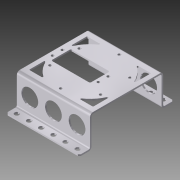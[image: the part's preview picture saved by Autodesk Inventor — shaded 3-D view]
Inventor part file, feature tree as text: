
AUTODESK INVENTOR PART (.ipt)
format: ipt  version: 2016 SP1 (Build 200210100, 210)  size: 432,128 bytes
history: native  units: in
note: dims shown in document units (in); Inventor stores cm internally (conversion verified against a paired STEP export)
features: sketch x9, other x7, extrude x4, sheet_metal_op x4, reference x4, projected_geometry x2, pattern_linear x1
ambient origin geometry x8: Origin, YZ Plane, XZ Plane, XY Plane, X Axis, Y Axis, Z Axis, Center Point
bodies: Solid1 (feature_tree)
feature tree (31):
  extrude  "Extrusion1"  Depth=2.875in
  extrude  "Extrusion2"  Depth=0.0625in
  sheet_metal_op  "Bend1"
  sheet_metal_op  "Bend2"
  extrude  "Extrusion3"  Depth=1.1875in TaperAngle=0.0deg
  sheet_metal_op  "Bend3"
  sheet_metal_op  "Bend4"
  other  "Corner Chamfer1"
  extrude  "Extrusion6"  Depth=0.0312in
  pattern_linear  "Rectangular Pattern1"  Spacing1=0.125in  [1 undecoded]
  sketch  "Sketch1"  dims[d0=3.0in d1=2.875in]
  sketch  "Sketch2"  dims[d2=0.0625in d3=0.0in d4=0.0625in]
  sketch  "Sketch3"  dims[d5=0.0625in d6=1.1875in d7=0.0in]
  projected_geometry  "Projected Loop1"
  sketch  "Sketch4"  dims[d8=0.0625in d9=0.0312in]
  projected_geometry  "Projected Loop2"
  sketch  "Sketch6"  dims[d10=0.125in]
  sketch  "Sketch7"  dims[d11=0.0625in]
  sketch  "Sketch8"  dims[d12=0.0625in]
  reference  "Reference1"
  reference  "Reference2"
  reference  "Reference3"
  reference  "Reference4"
  sketch  "Sketch9"  dims[d13=0.0625in]
  sketch  "Sketch12"  dims[d14=0.0312in d15=0.125in d16=0.0625in d17=0.0625in d18=0.4375in d19=0.4375in d20=0.0625in d21=0.0in d22=0.0625in d23=0.0312in d24=0.125in d25=0.0625in d26=0.0625in d27=0.0625in d28=0.0312in d29=0.125in d30=0.0625in d31=0.0625in d32=0.1875in d33=0.1875in d34=0.25in d35=0.25in d36=2.3622in d38=0.5in d39=0.3937in d41=1.0in d43=0.0625in d44=0.0in d57=0.1875in d58=0.0312in d59=0.0312in d60=0.0312in d61=0.0312in d62=0.0312in d63=0.0312in d64=0.3375in d65=0.0625in d66=0.0in d67=0.4016in d68=1.8819in d69=0.113in d71=0.5829in d72=0.0625in d73=0.0in d74=0.0625in d75=0.25in d76=45.0deg d78=0.0625in d79=0.0in d80=2.4in d81=0.113in d82=2.3622in d84=360.0deg d86=0.0625in d87=0.0in d92=0.688in d93=0.656in d94=0.531in d95=1.0in d96=0.0in d97=1.1811in d99=0.969in]
  other  "Cut1"
  other  "Cut3"
  other  "Cut4"
  other  "Cut5"
  other  "Cut6"
  other  "Definition1"
note: 1 required parameter value undecoded (feature->parameter linkage not recoverable at this tier; creation-order binding heuristic only, values carry confidence <= 0.55)
